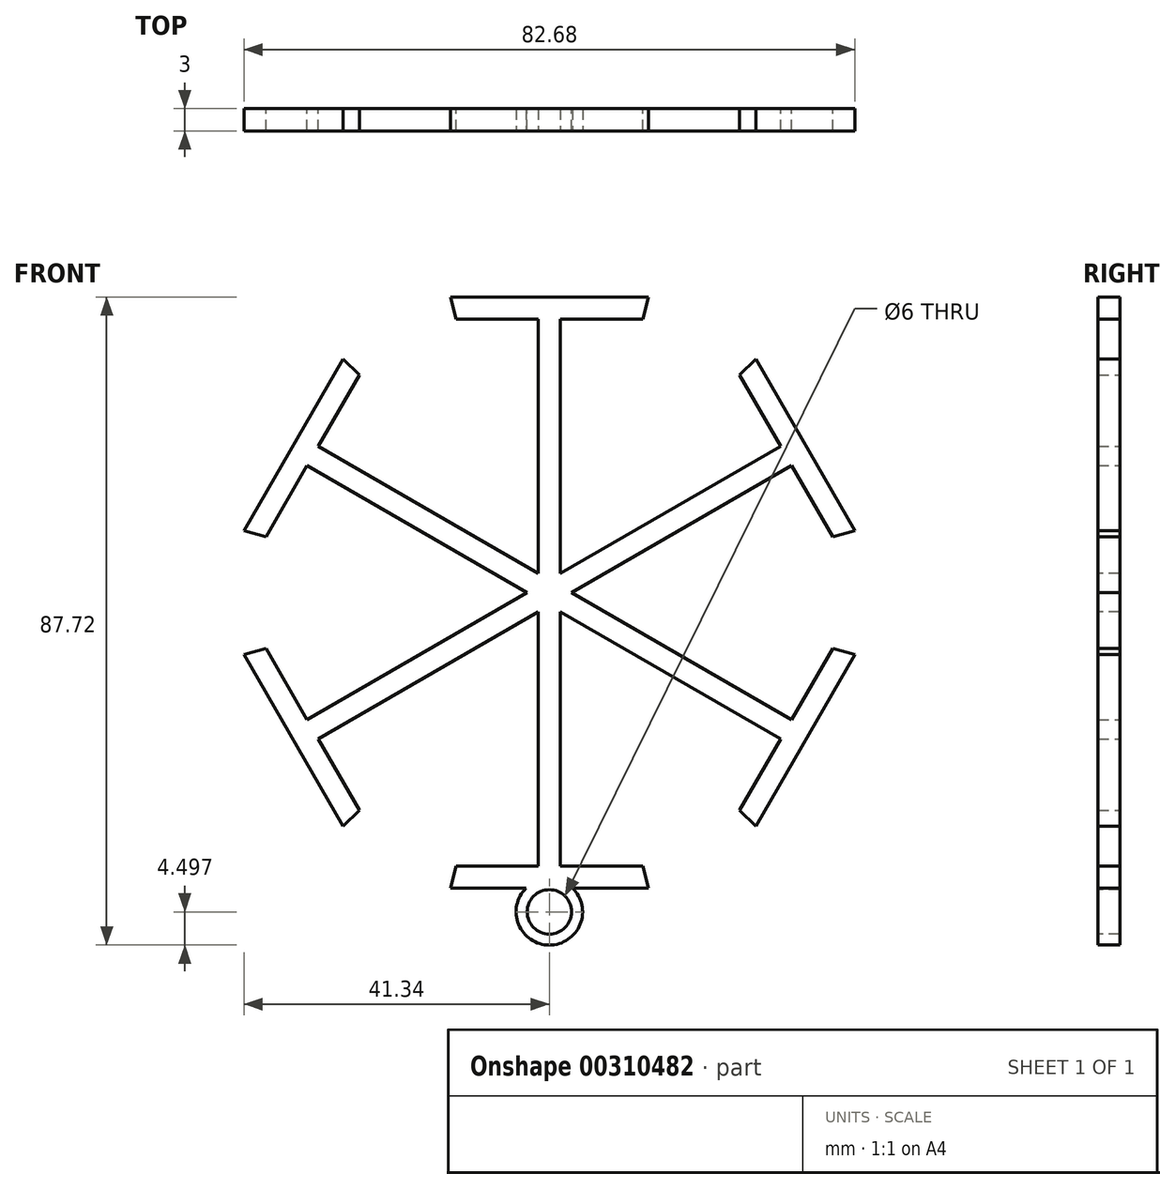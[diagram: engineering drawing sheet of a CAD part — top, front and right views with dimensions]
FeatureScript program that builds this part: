
annotation { "Feature Type Name" : "Feature", "Feature Type Description" : "" }
export const myFeature = defineFeature(function(context is Context, id is Id, definition is map)
    precondition{}
    {
        {
            var Q0;
            Q0=qCreatedBy(makeId("Front.planeOp"),FACE);
            var sketch = newSketch(context, id + "F0", { "sketchPlane" : qUnion([Q0])});
            skLineSegment(sketch, "E0.bottom", {"start": v(0, 0) * mm, "end": v(1.5, 0) * mm});
            skLineSegment(sketch, "E0.top", {"start": v(0, 40) * mm, "end": v(1.5, 40) * mm});
            skLineSegment(sketch, "E0.left", {"start": v(0, 0) * mm, "end": v(0, 40) * mm});
            skLineSegment(sketch, "E0.right", {"start": v(1.5, 0) * mm, "end": v(1.5, 40) * mm});
            skLineSegment(sketch, "E1.bottom", {"start": v(1.5, 40) * mm, "end": v(16.5, 40) * mm});
            skLineSegment(sketch, "E1.top", {"start": v(1.5, 37) * mm, "end": v(16.5, 37) * mm});
            skLineSegment(sketch, "E1.left", {"start": v(1.5, 40) * mm, "end": v(1.5, 37) * mm});
            skLineSegment(sketch, "E1.right", {"start": v(16.5, 40) * mm, "end": v(16.5, 37) * mm});
            skLineSegment(sketch, "E2.0.1.0", {"start": v(1.5, 33.1) * mm, "end": v(1.5, 30.1) * mm});
            skLineSegment(sketch, "E2.0.1.1", {"start": v(1.5, 33.1) * mm, "end": v(16.5, 33.1) * mm});
            skLineSegment(sketch, "E2.0.1.2", {"start": v(1.5, 30.1) * mm, "end": v(16.5, 30.1) * mm});
            skLineSegment(sketch, "E2.0.1.3", {"start": v(16.5, 33.1) * mm, "end": v(16.5, 30.1) * mm});
            skLineSegment(sketch, "E2.0.2.0", {"start": v(1.5, 26.2) * mm, "end": v(1.5, 23.2) * mm});
            skLineSegment(sketch, "E2.0.2.1", {"start": v(1.5, 26.2) * mm, "end": v(16.5, 26.2) * mm});
            skLineSegment(sketch, "E2.0.2.2", {"start": v(1.5, 23.2) * mm, "end": v(16.5, 23.2) * mm});
            skLineSegment(sketch, "E2.0.2.3", {"start": v(16.5, 26.2) * mm, "end": v(16.5, 23.2) * mm});
            skLineSegment(sketch, "E2.0.3.0", {"start": v(1.5, 19.3) * mm, "end": v(1.5, 16.3) * mm});
            skLineSegment(sketch, "E2.0.3.1", {"start": v(1.5, 19.3) * mm, "end": v(16.5, 19.3) * mm});
            skLineSegment(sketch, "E2.0.3.2", {"start": v(1.5, 16.3) * mm, "end": v(16.5, 16.3) * mm});
            skLineSegment(sketch, "E2.0.3.3", {"start": v(16.5, 19.3) * mm, "end": v(16.5, 16.3) * mm});
            skLineSegment(sketch, "E2.direction1", {"start": v(1.5, 37) * mm, "end": v(26.5, 37) * mm, "construction": true});
            skLineSegment(sketch, "E2.direction2", {"start": v(1.5, 37) * mm, "end": v(1.5, 30.1) * mm, "construction": true});
            skSolve(sketch);
        }
        {
            var Q0;
            Q0=makeQuery(id+"F0.imprint","IMPRINT",FACE,{"disambiguationData":[TD([[makeQuery(id+"F0.imprint","IMPRINT",EDGE,{"derivedFrom":sQuery(id+"F0.wireOp",EDGE,"E1.bottom")}),-1.0]])]});
            var Q1;
            Q1=makeQuery(id+"F0.imprint","IMPRINT",FACE,{"disambiguationData":[TD([[makeQuery(id+"F0.imprint","IMPRINT",EDGE,{"derivedFrom":sQuery(id+"F0.wireOp",EDGE,"E2.0.1.0")}),1.0]])]});
            var Q2;
            Q2=makeQuery(id+"F0.imprint","IMPRINT",FACE,{"disambiguationData":[TD([[makeQuery(id+"F0.imprint","IMPRINT",EDGE,{"derivedFrom":sQuery(id+"F0.wireOp",EDGE,"E2.0.2.0")}),1.0]])]});
            var Q3;
            Q3=makeQuery(id+"F0.imprint","IMPRINT",FACE,{"disambiguationData":[TD([[makeQuery(id+"F0.imprint","IMPRINT",EDGE,{"derivedFrom":sQuery(id+"F0.wireOp",EDGE,"E2.0.3.0")}),1.0]])]});
            var Q4;
            {var subQ5=sQuery(id+"F0.wireOp",EDGE,"E0.bottom");Q4=makeQuery(id+"F0.imprint","IMPRINT",FACE,{"disambiguationData":[TD([[makeQuery(id+"F0.imprint","IMPRINT",EDGE,{"derivedFrom":subQ5}),1.0]])]});}
            extrude(context, id + "F1", {"entities" : qUnion([Q0, Q1, Q2, Q3, Q4]), "depth" : 3 * mm});
        }
        {
            var Q0;
            Q0=makeQuery(id+"F1.opExtrude","CAP_FACE",FACE,{"disambiguationData":[OSD([sQuery(id+"F0.wireOp",EDGE,"E0.bottom"),sQuery(id+"F0.wireOp",EDGE,"E0.top"),sQuery(id+"F0.wireOp",EDGE,"E0.left"),sQuery(id+"F0.wireOp",EDGE,"E0.right"),sQuery(id+"F0.wireOp",EDGE,"E1.bottom"),sQuery(id+"F0.wireOp",EDGE,"E1.top"),sQuery(id+"F0.wireOp",EDGE,"E1.right"),sQuery(id+"F0.wireOp",EDGE,"E2.0.1.1"),sQuery(id+"F0.wireOp",EDGE,"E2.0.1.2"),sQuery(id+"F0.wireOp",EDGE,"E2.0.1.3"),sQuery(id+"F0.wireOp",EDGE,"E2.0.2.1"),sQuery(id+"F0.wireOp",EDGE,"E2.0.2.2"),sQuery(id+"F0.wireOp",EDGE,"E2.0.2.3"),sQuery(id+"F0.wireOp",EDGE,"E2.0.3.1"),sQuery(id+"F0.wireOp",EDGE,"E2.0.3.2"),sQuery(id+"F0.wireOp",EDGE,"E2.0.3.3")])],"isStart":false});
            var sketch = newSketch(context, id + "F2", { "sketchPlane" : qUnion([Q0])});
            skLineSegment(sketch, "E3", {"start": v(7.32, 16.3) * mm, "end": v(20.32, 16.3) * mm});
            skLineSegment(sketch, "E4", {"start": v(20.32, 16.3) * mm, "end": v(16.5, 40) * mm});
            skLineSegment(sketch, "E5", {"start": v(7.32, 16.3) * mm, "end": v(13.4, 40) * mm});
            skLineSegment(sketch, "E6", {"start": v(13.4, 40) * mm, "end": v(16.5, 40) * mm});
            skSolve(sketch);
        }
        {
            var Q0;
            Q0 = qSketchRegion(id + "F2", true);
            extrude(context, id + "F3", {"entities" : qUnion([Q0]), "operationType" : NewBodyOperationType.REMOVE, "oppositeDirection" : true, "depth" : 25 * mm});
        }
        {
            var Q0;
            Q0=makeQuery(id+"F1.opExtrude","SWEPT_BODY",BODY,{"disambiguationData":[OSD([sQuery(id+"F0.wireOp",EDGE,"E0.bottom"),sQuery(id+"F0.wireOp",EDGE,"E0.top"),sQuery(id+"F0.wireOp",EDGE,"E0.left"),sQuery(id+"F0.wireOp",EDGE,"E0.right"),sQuery(id+"F0.wireOp",EDGE,"E1.bottom"),sQuery(id+"F0.wireOp",EDGE,"E1.top"),sQuery(id+"F0.wireOp",EDGE,"E1.right"),sQuery(id+"F0.wireOp",EDGE,"E2.0.1.1"),sQuery(id+"F0.wireOp",EDGE,"E2.0.1.2"),sQuery(id+"F0.wireOp",EDGE,"E2.0.1.3"),sQuery(id+"F0.wireOp",EDGE,"E2.0.2.1"),sQuery(id+"F0.wireOp",EDGE,"E2.0.2.2"),sQuery(id+"F0.wireOp",EDGE,"E2.0.2.3"),sQuery(id+"F0.wireOp",EDGE,"E2.0.3.1"),sQuery(id+"F0.wireOp",EDGE,"E2.0.3.2"),sQuery(id+"F0.wireOp",EDGE,"E2.0.3.3")])]});
            var Q1;
            Q1=qCreatedBy(makeId("Right.planeOp"),FACE);
            mirror(context, id + "F4", {"operationType" : NewBodyOperationType.ADD, "entities" : qUnion([Q0]), "mirrorPlane" : qUnion([Q1])});
        }
        {
            var Q0;
            Q0=qCreatedBy(makeId("Right.planeOp"),FACE);
            var sketch = newSketch(context, id + "F5", { "sketchPlane" : qUnion([Q0])});
            skLineSegment(sketch, "E7", {"start": v(0, 0) * mm, "end": v(26.1, 0) * mm});
            skSolve(sketch);
        }
        {
            var Q0;
            Q0=makeQuery(id+"F1.opExtrude","SWEPT_BODY",BODY,{"disambiguationData":[OSD([sQuery(id+"F0.wireOp",EDGE,"E0.bottom"),sQuery(id+"F0.wireOp",EDGE,"E0.top"),sQuery(id+"F0.wireOp",EDGE,"E0.left"),sQuery(id+"F0.wireOp",EDGE,"E0.right"),sQuery(id+"F0.wireOp",EDGE,"E1.bottom"),sQuery(id+"F0.wireOp",EDGE,"E1.top"),sQuery(id+"F0.wireOp",EDGE,"E1.right"),sQuery(id+"F0.wireOp",EDGE,"E2.0.1.1"),sQuery(id+"F0.wireOp",EDGE,"E2.0.1.2"),sQuery(id+"F0.wireOp",EDGE,"E2.0.1.3"),sQuery(id+"F0.wireOp",EDGE,"E2.0.2.1"),sQuery(id+"F0.wireOp",EDGE,"E2.0.2.2"),sQuery(id+"F0.wireOp",EDGE,"E2.0.2.3"),sQuery(id+"F0.wireOp",EDGE,"E2.0.3.1"),sQuery(id+"F0.wireOp",EDGE,"E2.0.3.2"),sQuery(id+"F0.wireOp",EDGE,"E2.0.3.3")])]});
            var Q1;
            Q1=sQuery(id+"F5.wireOp",EDGE,"E7");
            circularPattern(context, id + "F6", {"entities" : qUnion([Q0]), "axis" : qUnion([Q1]), "angle" : 360 * degree, "instanceCount" : 6, "equalSpace" : true, "computeTransformsWithoutBuiltin" : true});
        }
        {
            var Q0;
            Q0=makeQuery(id+"F6.opPattern","COPY",BODY,{"derivedFrom":makeQuery(id+"F1.opExtrude","SWEPT_BODY",BODY,{"disambiguationData":[OSD([sQuery(id+"F0.wireOp",EDGE,"E0.bottom"),sQuery(id+"F0.wireOp",EDGE,"E0.top"),sQuery(id+"F0.wireOp",EDGE,"E0.left"),sQuery(id+"F0.wireOp",EDGE,"E0.right"),sQuery(id+"F0.wireOp",EDGE,"E1.bottom"),sQuery(id+"F0.wireOp",EDGE,"E1.top"),sQuery(id+"F0.wireOp",EDGE,"E1.right"),sQuery(id+"F0.wireOp",EDGE,"E2.0.1.1"),sQuery(id+"F0.wireOp",EDGE,"E2.0.1.2"),sQuery(id+"F0.wireOp",EDGE,"E2.0.1.3"),sQuery(id+"F0.wireOp",EDGE,"E2.0.2.1"),sQuery(id+"F0.wireOp",EDGE,"E2.0.2.2"),sQuery(id+"F0.wireOp",EDGE,"E2.0.2.3"),sQuery(id+"F0.wireOp",EDGE,"E2.0.3.1"),sQuery(id+"F0.wireOp",EDGE,"E2.0.3.2"),sQuery(id+"F0.wireOp",EDGE,"E2.0.3.3")])]}),"instanceName":"5"});
            var Q1;
            Q1=makeQuery(id+"F1.opExtrude","SWEPT_BODY",BODY,{"disambiguationData":[OSD([sQuery(id+"F0.wireOp",EDGE,"E0.bottom"),sQuery(id+"F0.wireOp",EDGE,"E0.top"),sQuery(id+"F0.wireOp",EDGE,"E0.left"),sQuery(id+"F0.wireOp",EDGE,"E0.right"),sQuery(id+"F0.wireOp",EDGE,"E1.bottom"),sQuery(id+"F0.wireOp",EDGE,"E1.top"),sQuery(id+"F0.wireOp",EDGE,"E1.right"),sQuery(id+"F0.wireOp",EDGE,"E2.0.1.1"),sQuery(id+"F0.wireOp",EDGE,"E2.0.1.2"),sQuery(id+"F0.wireOp",EDGE,"E2.0.1.3"),sQuery(id+"F0.wireOp",EDGE,"E2.0.2.1"),sQuery(id+"F0.wireOp",EDGE,"E2.0.2.2"),sQuery(id+"F0.wireOp",EDGE,"E2.0.2.3"),sQuery(id+"F0.wireOp",EDGE,"E2.0.3.1"),sQuery(id+"F0.wireOp",EDGE,"E2.0.3.2"),sQuery(id+"F0.wireOp",EDGE,"E2.0.3.3")])]});
            var Q2;
            Q2=makeQuery(id+"F6.opPattern","COPY",BODY,{"derivedFrom":makeQuery(id+"F1.opExtrude","SWEPT_BODY",BODY,{"disambiguationData":[OSD([sQuery(id+"F0.wireOp",EDGE,"E0.bottom"),sQuery(id+"F0.wireOp",EDGE,"E0.top"),sQuery(id+"F0.wireOp",EDGE,"E0.left"),sQuery(id+"F0.wireOp",EDGE,"E0.right"),sQuery(id+"F0.wireOp",EDGE,"E1.bottom"),sQuery(id+"F0.wireOp",EDGE,"E1.top"),sQuery(id+"F0.wireOp",EDGE,"E1.right"),sQuery(id+"F0.wireOp",EDGE,"E2.0.1.1"),sQuery(id+"F0.wireOp",EDGE,"E2.0.1.2"),sQuery(id+"F0.wireOp",EDGE,"E2.0.1.3"),sQuery(id+"F0.wireOp",EDGE,"E2.0.2.1"),sQuery(id+"F0.wireOp",EDGE,"E2.0.2.2"),sQuery(id+"F0.wireOp",EDGE,"E2.0.2.3"),sQuery(id+"F0.wireOp",EDGE,"E2.0.3.1"),sQuery(id+"F0.wireOp",EDGE,"E2.0.3.2"),sQuery(id+"F0.wireOp",EDGE,"E2.0.3.3")])]}),"instanceName":"2"});
            var Q3;
            Q3=makeQuery(id+"F6.opPattern","COPY",BODY,{"derivedFrom":makeQuery(id+"F1.opExtrude","SWEPT_BODY",BODY,{"disambiguationData":[OSD([sQuery(id+"F0.wireOp",EDGE,"E0.bottom"),sQuery(id+"F0.wireOp",EDGE,"E0.top"),sQuery(id+"F0.wireOp",EDGE,"E0.left"),sQuery(id+"F0.wireOp",EDGE,"E0.right"),sQuery(id+"F0.wireOp",EDGE,"E1.bottom"),sQuery(id+"F0.wireOp",EDGE,"E1.top"),sQuery(id+"F0.wireOp",EDGE,"E1.right"),sQuery(id+"F0.wireOp",EDGE,"E2.0.1.1"),sQuery(id+"F0.wireOp",EDGE,"E2.0.1.2"),sQuery(id+"F0.wireOp",EDGE,"E2.0.1.3"),sQuery(id+"F0.wireOp",EDGE,"E2.0.2.1"),sQuery(id+"F0.wireOp",EDGE,"E2.0.2.2"),sQuery(id+"F0.wireOp",EDGE,"E2.0.2.3"),sQuery(id+"F0.wireOp",EDGE,"E2.0.3.1"),sQuery(id+"F0.wireOp",EDGE,"E2.0.3.2"),sQuery(id+"F0.wireOp",EDGE,"E2.0.3.3")])]}),"instanceName":"3"});
            var Q4;
            Q4=makeQuery(id+"F6.opPattern","COPY",BODY,{"derivedFrom":makeQuery(id+"F1.opExtrude","SWEPT_BODY",BODY,{"disambiguationData":[OSD([sQuery(id+"F0.wireOp",EDGE,"E0.bottom"),sQuery(id+"F0.wireOp",EDGE,"E0.top"),sQuery(id+"F0.wireOp",EDGE,"E0.left"),sQuery(id+"F0.wireOp",EDGE,"E0.right"),sQuery(id+"F0.wireOp",EDGE,"E1.bottom"),sQuery(id+"F0.wireOp",EDGE,"E1.top"),sQuery(id+"F0.wireOp",EDGE,"E1.right"),sQuery(id+"F0.wireOp",EDGE,"E2.0.1.1"),sQuery(id+"F0.wireOp",EDGE,"E2.0.1.2"),sQuery(id+"F0.wireOp",EDGE,"E2.0.1.3"),sQuery(id+"F0.wireOp",EDGE,"E2.0.2.1"),sQuery(id+"F0.wireOp",EDGE,"E2.0.2.2"),sQuery(id+"F0.wireOp",EDGE,"E2.0.2.3"),sQuery(id+"F0.wireOp",EDGE,"E2.0.3.1"),sQuery(id+"F0.wireOp",EDGE,"E2.0.3.2"),sQuery(id+"F0.wireOp",EDGE,"E2.0.3.3")])]}),"instanceName":"4"});
            var Q5;
            Q5=makeQuery(id+"F6.opPattern","COPY",BODY,{"derivedFrom":makeQuery(id+"F1.opExtrude","SWEPT_BODY",BODY,{"disambiguationData":[OSD([sQuery(id+"F0.wireOp",EDGE,"E0.bottom"),sQuery(id+"F0.wireOp",EDGE,"E0.top"),sQuery(id+"F0.wireOp",EDGE,"E0.left"),sQuery(id+"F0.wireOp",EDGE,"E0.right"),sQuery(id+"F0.wireOp",EDGE,"E1.bottom"),sQuery(id+"F0.wireOp",EDGE,"E1.top"),sQuery(id+"F0.wireOp",EDGE,"E1.right"),sQuery(id+"F0.wireOp",EDGE,"E2.0.1.1"),sQuery(id+"F0.wireOp",EDGE,"E2.0.1.2"),sQuery(id+"F0.wireOp",EDGE,"E2.0.1.3"),sQuery(id+"F0.wireOp",EDGE,"E2.0.2.1"),sQuery(id+"F0.wireOp",EDGE,"E2.0.2.2"),sQuery(id+"F0.wireOp",EDGE,"E2.0.2.3"),sQuery(id+"F0.wireOp",EDGE,"E2.0.3.1"),sQuery(id+"F0.wireOp",EDGE,"E2.0.3.2"),sQuery(id+"F0.wireOp",EDGE,"E2.0.3.3")])]}),"instanceName":"1"});
            booleanBodies(context, id + "F7", {"operationType" : BooleanOperationType.UNION, "tools" : qUnion([Q0, Q1, Q2, Q3, Q4, Q5])});
        }
        {
            var Q0;
            {var subQ0=makeQuery(id+"F1.opExtrude","CAP_FACE",FACE,{"disambiguationData":[OSD([sQuery(id+"F0.wireOp",EDGE,"E0.bottom"),sQuery(id+"F0.wireOp",EDGE,"E0.top"),sQuery(id+"F0.wireOp",EDGE,"E0.left"),sQuery(id+"F0.wireOp",EDGE,"E0.right"),sQuery(id+"F0.wireOp",EDGE,"E1.bottom"),sQuery(id+"F0.wireOp",EDGE,"E1.top"),sQuery(id+"F0.wireOp",EDGE,"E1.right"),sQuery(id+"F0.wireOp",EDGE,"E2.0.1.1"),sQuery(id+"F0.wireOp",EDGE,"E2.0.1.2"),sQuery(id+"F0.wireOp",EDGE,"E2.0.1.3"),sQuery(id+"F0.wireOp",EDGE,"E2.0.2.1"),sQuery(id+"F0.wireOp",EDGE,"E2.0.2.2"),sQuery(id+"F0.wireOp",EDGE,"E2.0.2.3"),sQuery(id+"F0.wireOp",EDGE,"E2.0.3.1"),sQuery(id+"F0.wireOp",EDGE,"E2.0.3.2"),sQuery(id+"F0.wireOp",EDGE,"E2.0.3.3")])],"isStart":false});var subQ1=makeQuery(id+"F4.boolean.opBoolean","MERGE",FACE,{"derivedFrom":[subQ0,makeQuery(id+"F4.opPattern","COPY",FACE,{"derivedFrom":subQ0,"instanceName":"1"})]});Q0=makeQuery(id+"F7.opBoolean","MERGE",FACE,{"derivedFrom":[subQ1,makeQuery(id+"F6.opPattern","COPY",FACE,{"derivedFrom":subQ1,"instanceName":"1"}),makeQuery(id+"F6.opPattern","COPY",FACE,{"derivedFrom":subQ1,"instanceName":"2"}),makeQuery(id+"F6.opPattern","COPY",FACE,{"derivedFrom":subQ1,"instanceName":"3"}),makeQuery(id+"F6.opPattern","COPY",FACE,{"derivedFrom":subQ1,"instanceName":"4"}),makeQuery(id+"F6.opPattern","COPY",FACE,{"derivedFrom":subQ1,"instanceName":"5"})]});}
            var sketch = newSketch(context, id + "F8", { "sketchPlane" : qUnion([Q0])});
            skCircle(sketch, "E8", {"center": v(0, -43.22) * mm, "radius": 4.5 * mm});
            skPoint(sketch, "E8.centerSnap0", {"position": v(0, -40) * mm});
            skCircle(sketch, "E9", {"center": v(0, -43.22) * mm, "radius": 3 * mm});
            skSolve(sketch);
        }
        {
            var Q0;
            Q0=makeQuery(id+"F8.imprint","IMPRINT",FACE,{"disambiguationData":[TD([[makeQuery(id+"F8.imprint","IMPRINT",EDGE,{"derivedFrom":sQuery(id+"F8.wireOp",EDGE,"E9")}),-1.0]])]});
            var Q1;
            {var subQ0=makeQuery(id+"F1.opExtrude","CAP_FACE",FACE,{"disambiguationData":[OSD([sQuery(id+"F0.wireOp",EDGE,"E0.bottom"),sQuery(id+"F0.wireOp",EDGE,"E0.top"),sQuery(id+"F0.wireOp",EDGE,"E0.left"),sQuery(id+"F0.wireOp",EDGE,"E0.right"),sQuery(id+"F0.wireOp",EDGE,"E1.bottom"),sQuery(id+"F0.wireOp",EDGE,"E1.top"),sQuery(id+"F0.wireOp",EDGE,"E1.right"),sQuery(id+"F0.wireOp",EDGE,"E2.0.1.1"),sQuery(id+"F0.wireOp",EDGE,"E2.0.1.2"),sQuery(id+"F0.wireOp",EDGE,"E2.0.1.3"),sQuery(id+"F0.wireOp",EDGE,"E2.0.2.1"),sQuery(id+"F0.wireOp",EDGE,"E2.0.2.2"),sQuery(id+"F0.wireOp",EDGE,"E2.0.2.3"),sQuery(id+"F0.wireOp",EDGE,"E2.0.3.1"),sQuery(id+"F0.wireOp",EDGE,"E2.0.3.2"),sQuery(id+"F0.wireOp",EDGE,"E2.0.3.3")])],"isStart":true});var subQ1=makeQuery(id+"F4.boolean.opBoolean","MERGE",FACE,{"derivedFrom":[subQ0,makeQuery(id+"F4.opPattern","COPY",FACE,{"derivedFrom":subQ0,"instanceName":"1"})]});Q1=makeQuery(id+"F7.opBoolean","MERGE",FACE,{"derivedFrom":[subQ1,makeQuery(id+"F6.opPattern","COPY",FACE,{"derivedFrom":subQ1,"instanceName":"1"}),makeQuery(id+"F6.opPattern","COPY",FACE,{"derivedFrom":subQ1,"instanceName":"2"}),makeQuery(id+"F6.opPattern","COPY",FACE,{"derivedFrom":subQ1,"instanceName":"3"}),makeQuery(id+"F6.opPattern","COPY",FACE,{"derivedFrom":subQ1,"instanceName":"4"}),makeQuery(id+"F6.opPattern","COPY",FACE,{"derivedFrom":subQ1,"instanceName":"5"})]});}
            extrude(context, id + "F9", {"entities" : qUnion([Q0]), "operationType" : NewBodyOperationType.ADD, "endBound" : BoundingType.UP_TO_SURFACE, "oppositeDirection" : true, "endBoundEntityFace" : qUnion([Q1]), "depth" : 25 * mm});
        }
    });
